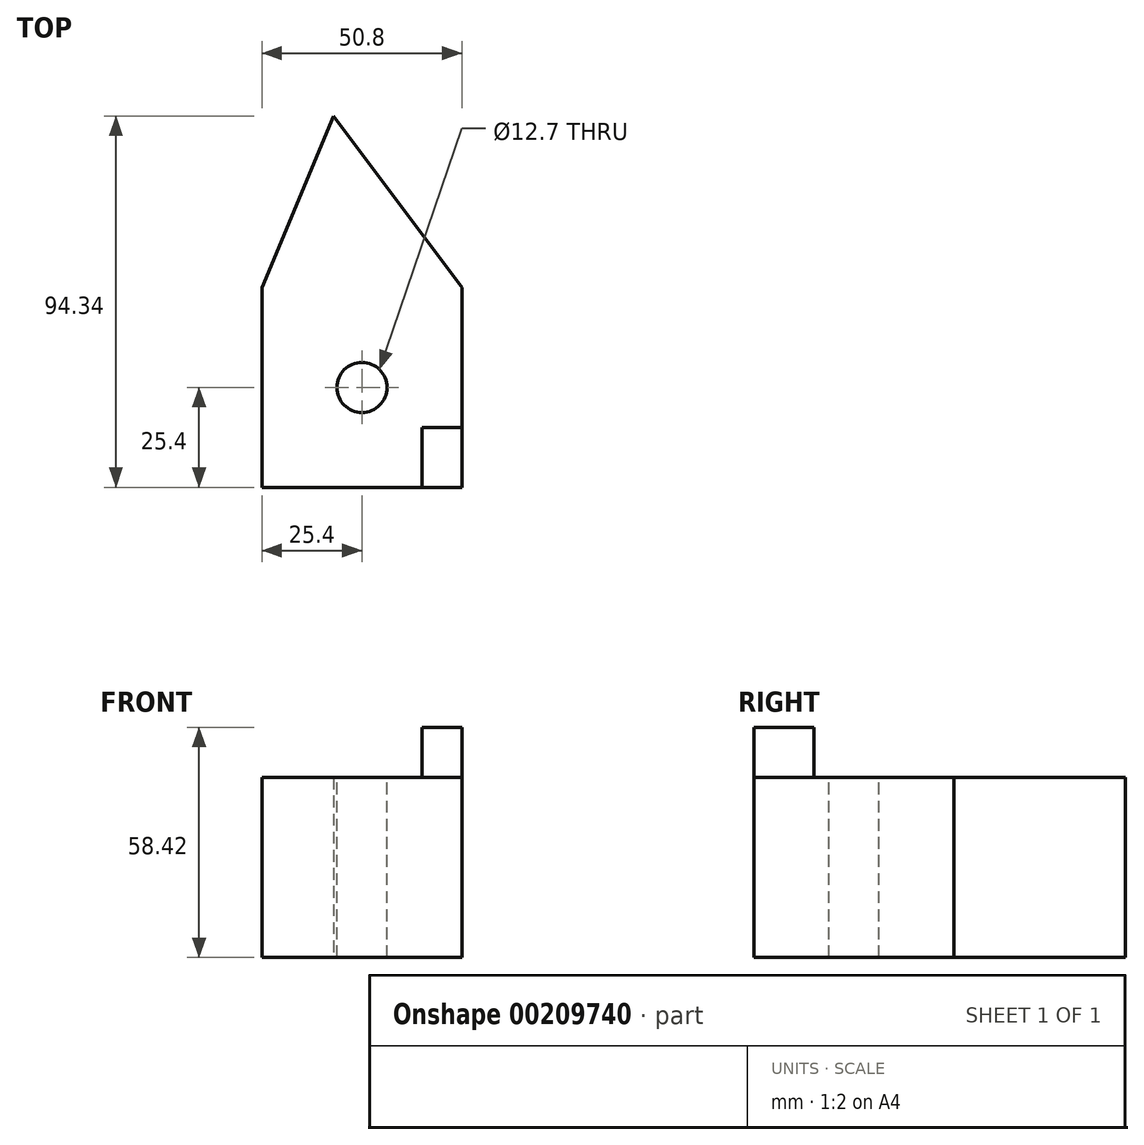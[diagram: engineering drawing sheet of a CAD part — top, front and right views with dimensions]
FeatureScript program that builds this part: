
annotation { "Feature Type Name" : "Feature", "Feature Type Description" : "" }
export const myFeature = defineFeature(function(context is Context, id is Id, definition is map)
    precondition{}
    {
        {
            var Q0;
            Q0=qCreatedBy(makeId("Top.planeOp"),FACE);
            var sketch = newSketch(context, id + "F0", { "sketchPlane" : qUnion([Q0])});
            skLineSegment(sketch, "E0.bottom", {"start": v(0, 0) * mm, "end": v(50.8, 0) * mm});
            skLineSegment(sketch, "E0.top", {"start": v(0, 50.8) * mm, "end": v(50.8, 50.8) * mm});
            skLineSegment(sketch, "E0.left", {"start": v(0, 0) * mm, "end": v(0, 50.8) * mm});
            skLineSegment(sketch, "E0.right", {"start": v(50.8, 0) * mm, "end": v(50.8, 50.8) * mm});
            skLineSegment(sketch, "E1", {"start": v(0, 50.8) * mm, "end": v(18.14, 94.34) * mm});
            skLineSegment(sketch, "E2", {"start": v(18.14, 94.34) * mm, "end": v(50.8, 50.8) * mm});
            skSolve(sketch);
        }
        {
            var Q0;
            Q0 = qSketchRegion(id + "F0", true);
            extrude(context, id + "F1", {"entities" : qUnion([Q0]), "depth" : 45.72 * mm});
        }
        {
            var Q0;
            Q0=makeQuery(id+"F1.opExtrude","CAP_FACE",FACE,{"disambiguationData":[OSD([sQuery(id+"F0.wireOp",EDGE,"E0.bottom"),sQuery(id+"F0.wireOp",EDGE,"E0.left"),sQuery(id+"F0.wireOp",EDGE,"E0.right"),sQuery(id+"F0.wireOp",EDGE,"E1"),sQuery(id+"F0.wireOp",EDGE,"E2")])],"isStart":false});
            var sketch = newSketch(context, id + "F2", { "sketchPlane" : qUnion([Q0])});
            skCircle(sketch, "E3", {"center": v(25.4, 25.4) * mm, "radius": 6.35 * mm});
            skSolve(sketch);
        }
        {
            var Q0;
            Q0 = qSketchRegion(id + "F2", true);
            extrude(context, id + "F3", {"entities" : qUnion([Q0]), "operationType" : NewBodyOperationType.REMOVE, "endBound" : BoundingType.THROUGH_ALL, "oppositeDirection" : true, "depth" : 25.4 * mm});
        }
        {
            var Q0;
            Q0=makeQuery(id+"F1.opExtrude","CAP_FACE",FACE,{"disambiguationData":[OSD([sQuery(id+"F0.wireOp",EDGE,"E0.bottom"),sQuery(id+"F0.wireOp",EDGE,"E0.left"),sQuery(id+"F0.wireOp",EDGE,"E0.right"),sQuery(id+"F0.wireOp",EDGE,"E1"),sQuery(id+"F0.wireOp",EDGE,"E2")])],"isStart":false});
            var sketch = newSketch(context, id + "F4", { "sketchPlane" : qUnion([Q0])});
            skLineSegment(sketch, "E4.bottom", {"start": v(50.8, 0) * mm, "end": v(40.64, 0) * mm});
            skLineSegment(sketch, "E4.top", {"start": v(50.8, 15.24) * mm, "end": v(40.64, 15.24) * mm});
            skLineSegment(sketch, "E4.left", {"start": v(50.8, 0) * mm, "end": v(50.8, 15.24) * mm});
            skLineSegment(sketch, "E4.right", {"start": v(40.64, 0) * mm, "end": v(40.64, 15.24) * mm});
            skSolve(sketch);
        }
        {
            var Q0;
            Q0 = qSketchRegion(id + "F4", true);
            extrude(context, id + "F5", {"entities" : qUnion([Q0]), "depth" : 12.7 * mm});
        }
    });
